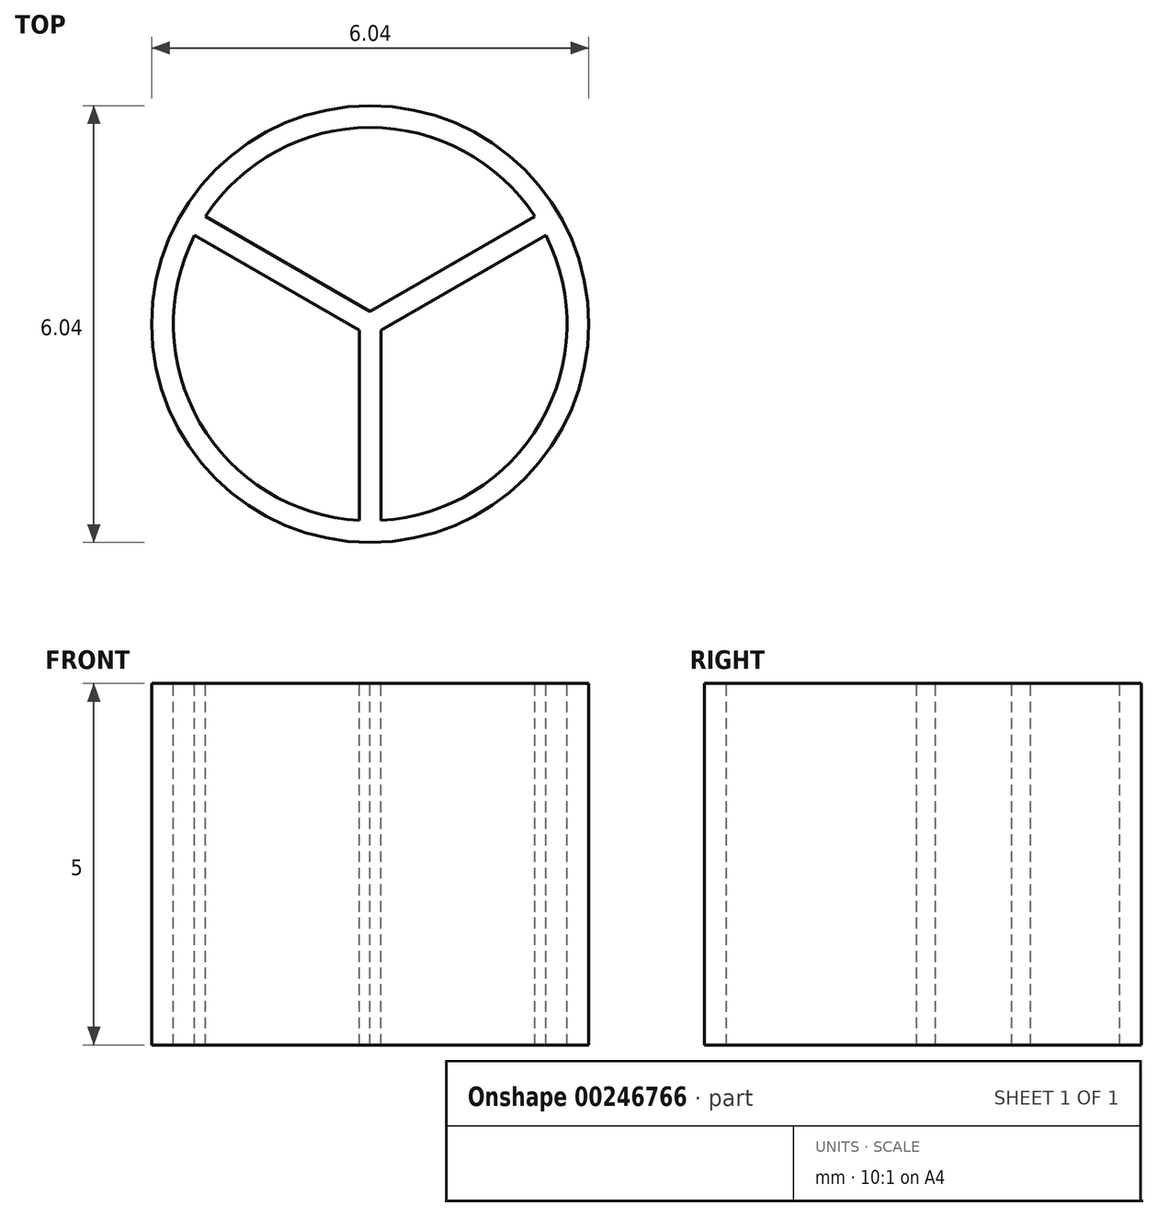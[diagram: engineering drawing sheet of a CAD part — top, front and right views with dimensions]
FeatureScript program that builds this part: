
annotation { "Feature Type Name" : "Feature", "Feature Type Description" : "" }
export const myFeature = defineFeature(function(context is Context, id is Id, definition is map)
    precondition{}
    {
        {
            var Q0;
            Q0=qCreatedBy(makeId("Top.planeOp"),FACE);
            var sketch = newSketch(context, id + "F0", { "sketchPlane" : qUnion([Q0])});
            skCircle(sketch, "E0", {"center": v(0, 0) * mm, "radius": 3.02 * mm});
            skSolve(sketch);
        }
        {
            var Q0;
            Q0=makeQuery(id+"F0.imprint","IMPRINT",FACE,{"disambiguationData":[TD([[makeQuery(id+"F0.imprint","IMPRINT",EDGE,{"derivedFrom":sQuery(id+"F0.wireOp",EDGE,"E0")}),1.0]])]});
            extrude(context, id + "F1", {"entities" : qUnion([Q0]), "depth" : 5 * mm});
        }
        {
            var Q0;
            Q0=makeQuery(id+"F1.opExtrude","CAP_FACE",FACE,{"disambiguationData":[OSD([sQuery(id+"F0.wireOp",EDGE,"E0")])],"isStart":false});
            var sketch = newSketch(context, id + "F2", { "sketchPlane" : qUnion([Q0])});
            skCircle(sketch, "E1", {"center": v(0, 0) * mm, "radius": 2.72 * mm});
            skCircle(sketch, "E2.cCircle", {"center": v(0, 2.72) * mm, "radius": 2.72 * mm, "construction": true});
            skLineSegment(sketch, "E2.0", {"start": v(0, 0) * mm, "end": v(-2.36, 1.36) * mm});
            skLineSegment(sketch, "E2.1", {"start": v(-2.36, 1.36) * mm, "end": v(-2.36, 4.08) * mm});
            skLineSegment(sketch, "E2.2", {"start": v(-2.36, 4.08) * mm, "end": v(0, 5.44) * mm});
            skLineSegment(sketch, "E2.3", {"start": v(0, 5.44) * mm, "end": v(2.36, 4.08) * mm});
            skLineSegment(sketch, "E2.4", {"start": v(2.36, 4.08) * mm, "end": v(2.36, 1.36) * mm});
            skLineSegment(sketch, "E2.5", {"start": v(2.36, 1.36) * mm, "end": v(0, 0) * mm});
            skLineSegment(sketch, "E3.1.0", {"start": v(-2.36, -4.08) * mm, "end": v(-4.71, -2.72) * mm});
            skLineSegment(sketch, "E3.1.1", {"start": v(-4.71, -2.72) * mm, "end": v(-4.71, 0) * mm});
            skLineSegment(sketch, "E3.1.2", {"start": v(-4.71, 0) * mm, "end": v(-2.36, 1.36) * mm});
            skLineSegment(sketch, "E3.1.3", {"start": v(-2.36, 1.36) * mm, "end": v(0, 0) * mm});
            skLineSegment(sketch, "E3.1.4", {"start": v(0, 0) * mm, "end": v(0, -2.72) * mm});
            skLineSegment(sketch, "E3.1.5", {"start": v(0, -2.72) * mm, "end": v(-2.36, -4.08) * mm});
            skLineSegment(sketch, "E3.2.0", {"start": v(4.71, 0) * mm, "end": v(4.71, -2.72) * mm});
            skLineSegment(sketch, "E3.2.1", {"start": v(4.71, -2.72) * mm, "end": v(2.36, -4.08) * mm});
            skLineSegment(sketch, "E3.2.2", {"start": v(2.36, -4.08) * mm, "end": v(0, -2.72) * mm});
            skLineSegment(sketch, "E3.2.3", {"start": v(0, -2.72) * mm, "end": v(0, 0) * mm});
            skLineSegment(sketch, "E3.2.4", {"start": v(0, 0) * mm, "end": v(2.36, 1.36) * mm});
            skLineSegment(sketch, "E3.2.5", {"start": v(2.36, 1.36) * mm, "end": v(4.71, 0) * mm});
            skLineSegment(sketch, "E4.0", {"start": v(0.06, 0.14) * mm, "end": v(-2.28, 1.49) * mm});
            skCircle(sketch, "E5.0", {"center": v(0, 0) * mm, "radius": 8.02 * mm});
            skLineSegment(sketch, "E6.0", {"start": v(-0.1, -0.12) * mm, "end": v(-2.43, 1.23) * mm});
            skLineSegment(sketch, "E7.0", {"start": v(0.15, -2.72) * mm, "end": v(0.15, 0) * mm});
            skLineSegment(sketch, "E8.0", {"start": v(-0.15, -2.72) * mm, "end": v(-0.15, 0) * mm});
            skLineSegment(sketch, "E9.0", {"start": v(0.07, -0.13) * mm, "end": v(2.43, 1.23) * mm});
            skLineSegment(sketch, "E10.0", {"start": v(-0.08, 0.13) * mm, "end": v(2.28, 1.49) * mm});
            skSolve(sketch);
        }
        {
            var Q0;
            {var subQ0=sQuery(id+"F2.wireOp",EDGE,"E6.0");var subQ1=sQuery(id+"F2.wireOp",EDGE,"E1");var subQ2=makeQuery(id+"F2.imprint","INTERSECT",VERTEX,{"derivedFrom":[subQ1,subQ0]});Q0=makeQuery(id+"F2.imprint","IMPRINT",FACE,{"disambiguationData":[TD([[makeQuery(id+"F2.imprint","IMPRINT",EDGE,{"disambiguationData":[TD([[subQ2,-1.0]])],"derivedFrom":subQ1}),1.0]])]});}
            var Q1;
            {var subQ0=sQuery(id+"F2.wireOp",EDGE,"E10.0");var subQ1=sQuery(id+"F2.wireOp",EDGE,"E1");var subQ2=makeQuery(id+"F2.imprint","INTERSECT",VERTEX,{"derivedFrom":[subQ1,subQ0]});Q1=makeQuery(id+"F2.imprint","IMPRINT",FACE,{"disambiguationData":[TD([[makeQuery(id+"F2.imprint","IMPRINT",EDGE,{"disambiguationData":[TD([[subQ2,-1.0]])],"derivedFrom":subQ1}),1.0]])]});}
            var Q2;
            {var subQ0=sQuery(id+"F2.wireOp",EDGE,"E9.0");var subQ1=sQuery(id+"F2.wireOp",EDGE,"E1");var subQ2=makeQuery(id+"F2.imprint","INTERSECT",VERTEX,{"derivedFrom":[subQ1,subQ0]});Q2=makeQuery(id+"F2.imprint","IMPRINT",FACE,{"disambiguationData":[TD([[makeQuery(id+"F2.imprint","IMPRINT",EDGE,{"disambiguationData":[TD([[subQ2,1.0]])],"derivedFrom":subQ1}),1.0]])]});}
            extrude(context, id + "F3", {"entities" : qUnion([Q0, Q1, Q2]), "operationType" : NewBodyOperationType.REMOVE, "oppositeDirection" : true, "depth" : 5 * mm});
        }
    });
